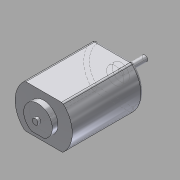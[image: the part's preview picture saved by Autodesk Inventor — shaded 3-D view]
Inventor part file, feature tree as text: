
AUTODESK INVENTOR PART (.ipt)
format: ipt  version: 2015 (Build 190159000, 159)  size: 138,240 bytes
history: native  units: in
note: dims shown in document units (in); Inventor stores cm internally (conversion verified against a paired STEP export)
features: sketch x5, other x3
ambient origin geometry x8: Origin, YZ Plane, XZ Plane, XY Plane, X Axis, Y Axis, Z Axis, Center Point
bodies: Solid1 (feature_tree)
feature tree (8):
  other  "motor.ipt"
  other  "Solid1::motor.ipt"
  other  "TaggingFeature1"
  sketch  "Sketch1"  dims[d0=0.3937in]
  sketch  "Sketch2"
  sketch  "Sketch3"
  sketch  "Sketch4"
  sketch  "Sketch5"
